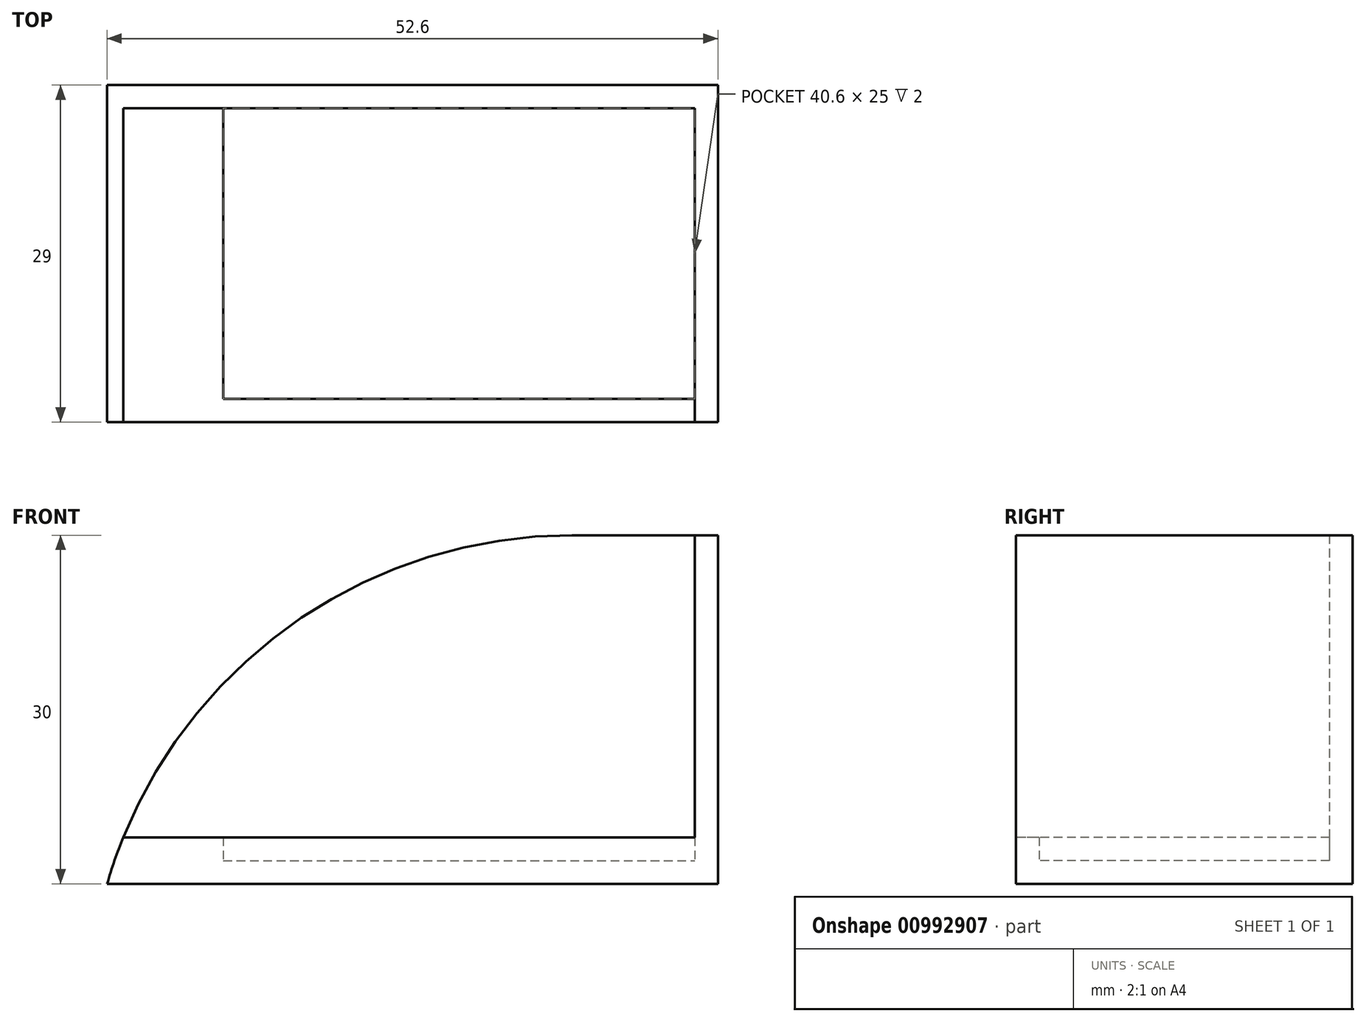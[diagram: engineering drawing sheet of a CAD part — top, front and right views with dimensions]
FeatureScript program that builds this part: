
annotation { "Feature Type Name" : "Feature", "Feature Type Description" : "" }
export const myFeature = defineFeature(function(context is Context, id is Id, definition is map)
    precondition{}
    {
        {
            var Q0;
            Q0=qCreatedBy(makeId("Top.planeOp"),FACE);
            var sketch = newSketch(context, id + "F0", { "sketchPlane" : qUnion([Q0])});
            skLineSegment(sketch, "E0.bottom", {"start": v(3.73, -3.66) * mm, "end": v(44.33, -3.66) * mm});
            skLineSegment(sketch, "E0.top", {"start": v(3.73, -28.66) * mm, "end": v(44.33, -28.66) * mm});
            skLineSegment(sketch, "E0.left", {"start": v(3.73, -3.66) * mm, "end": v(3.73, -28.66) * mm});
            skLineSegment(sketch, "E0.right", {"start": v(44.33, -3.66) * mm, "end": v(44.33, -28.66) * mm});
            skLineSegment(sketch, "E1.bottom", {"start": v(3.73, -3.66) * mm, "end": v(-6.27, -3.66) * mm});
            skLineSegment(sketch, "E1.top", {"start": v(3.73, -28.66) * mm, "end": v(-6.27, -28.66) * mm});
            skLineSegment(sketch, "E1.right", {"start": v(-6.27, -3.66) * mm, "end": v(-6.27, -28.66) * mm});
            skLineSegment(sketch, "E2.bottom", {"start": v(-6.27, -28.66) * mm, "end": v(44.33, -28.66) * mm});
            skLineSegment(sketch, "E2.top", {"start": v(-6.27, -30.66) * mm, "end": v(44.33, -30.66) * mm});
            skLineSegment(sketch, "E2.left", {"start": v(-6.27, -28.66) * mm, "end": v(-6.27, -30.66) * mm});
            skLineSegment(sketch, "E2.right", {"start": v(44.33, -28.66) * mm, "end": v(44.33, -30.66) * mm});
            skLineSegment(sketch, "E3.bottom", {"start": v(-6.27, -3.66) * mm, "end": v(44.33, -3.66) * mm});
            skLineSegment(sketch, "E3.top", {"start": v(-6.27, -1.66) * mm, "end": v(44.33, -1.66) * mm});
            skLineSegment(sketch, "E3.left", {"start": v(-6.27, -3.66) * mm, "end": v(-6.27, -1.66) * mm});
            skLineSegment(sketch, "E3.right", {"start": v(44.33, -3.66) * mm, "end": v(44.33, -1.66) * mm});
            skLineSegment(sketch, "E4.bottom", {"start": v(44.33, -1.66) * mm, "end": v(46.33, -1.66) * mm});
            skLineSegment(sketch, "E4.top", {"start": v(44.33, -30.66) * mm, "end": v(46.33, -30.66) * mm});
            skLineSegment(sketch, "E4.left", {"start": v(44.33, -1.66) * mm, "end": v(44.33, -30.66) * mm});
            skLineSegment(sketch, "E4.right", {"start": v(46.33, -1.66) * mm, "end": v(46.33, -30.66) * mm});
            skSolve(sketch);
        }
        {
            var Q0;
            Q0=makeQuery(id+"F0.imprint","IMPRINT",FACE,{"disambiguationData":[TD([[makeQuery(id+"F0.imprint","IMPRINT",EDGE,{"derivedFrom":sQuery(id+"F0.wireOp",EDGE,"E0.bottom")}),-1.0]])]});
            extrude(context, id + "F1", {"entities" : qUnion([Q0]), "depth" : 2 * mm, "offsetDistance" : 25.4 * mm});
        }
        {
            var Q0;
            Q0=makeQuery(id+"F0.imprint","IMPRINT",FACE,{"disambiguationData":[TD([[makeQuery(id+"F0.imprint","IMPRINT",EDGE,{"derivedFrom":sQuery(id+"F0.wireOp",EDGE,"E0.right")}),1.0]])]});
            extrude(context, id + "F2", {"entities" : qUnion([Q0]), "operationType" : NewBodyOperationType.ADD, "depth" : 30 * mm, "offsetDistance" : 25.4 * mm});
        }
        {
            var Q0;
            Q0=makeQuery(id+"F0.imprint","IMPRINT",FACE,{"disambiguationData":[TD([[makeQuery(id+"F0.imprint","IMPRINT",EDGE,{"derivedFrom":sQuery(id+"F0.wireOp",EDGE,"E0.top")}),-1.0]])]});
            extrude(context, id + "F3", {"entities" : qUnion([Q0]), "operationType" : NewBodyOperationType.ADD, "depth" : 4 * mm, "offsetDistance" : 25.4 * mm});
        }
        {
            var Q0;
            Q0=makeQuery(id+"F0.imprint","IMPRINT",FACE,{"disambiguationData":[TD([[makeQuery(id+"F0.imprint","IMPRINT",EDGE,{"derivedFrom":sQuery(id+"F0.wireOp",EDGE,"E0.bottom")}),1.0]])]});
            extrude(context, id + "F4", {"entities" : qUnion([Q0]), "operationType" : NewBodyOperationType.ADD, "depth" : 30 * mm, "offsetDistance" : 25.4 * mm});
        }
        {
            var Q0;
            Q0=makeQuery(id+"F0.imprint","IMPRINT",FACE,{"disambiguationData":[TD([[makeQuery(id+"F0.imprint","IMPRINT",EDGE,{"derivedFrom":sQuery(id+"F0.wireOp",EDGE,"E0.left")}),-1.0]])]});
            extrude(context, id + "F5", {"entities" : qUnion([Q0]), "operationType" : NewBodyOperationType.ADD, "depth" : 4 * mm, "offsetDistance" : 25.4 * mm});
        }
        {
            var Q0;
            Q0=makeQuery(id+"F4.opExtrude","CAP_EDGE",EDGE,{"disambiguationData":[OSD([sQuery(id+"F0.wireOp",EDGE,"E3.left")])],"isStart":false});
            fillet(context, id + "F6", {"entities" : qUnion([Q0]), "radius" : 41.7 * mm, "tangentPropagation" : true, "allowEdgeOverflow" : false});
        }
    });
